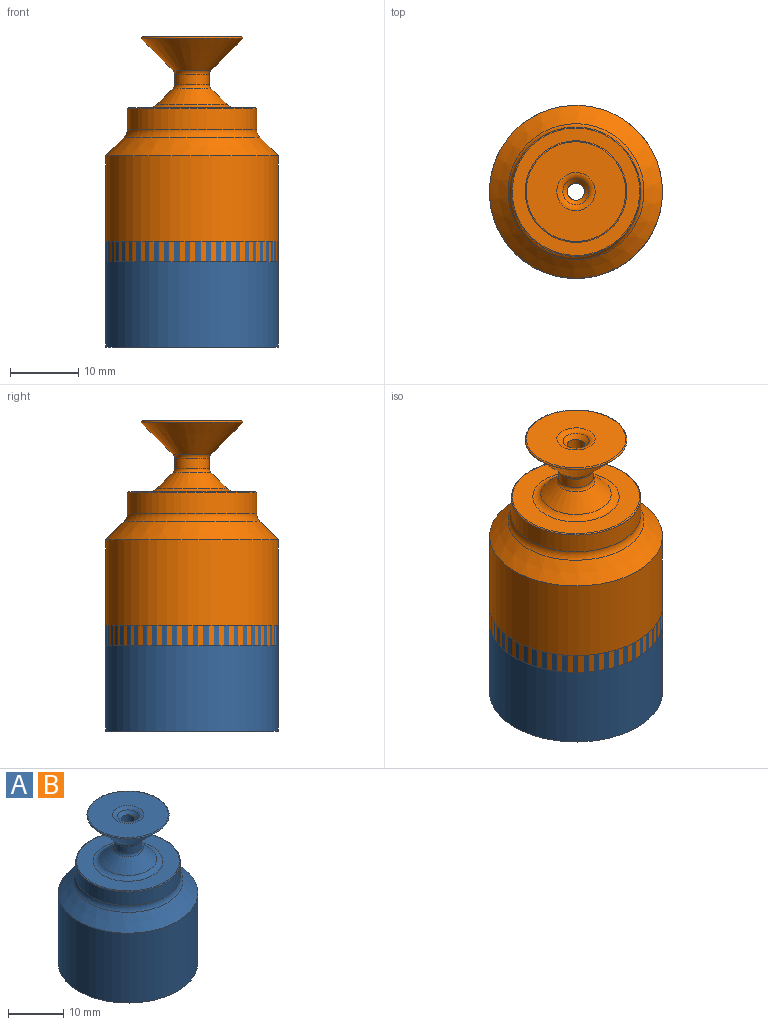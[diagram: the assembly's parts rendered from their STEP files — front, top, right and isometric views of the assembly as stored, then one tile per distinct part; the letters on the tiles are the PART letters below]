
ASSEMBLY  parts=2 mates=1
PART A: 28 faces, bbox 25.4x25.4x33 mm
  f0: cone r=7.88mm half-angle=45deg, axis (0,0,-1), area 268.9mm2, adj f4,f27
  f1: cone r=1.92mm half-angle=45deg, axis (0,0,1), area 9.2mm2, adj f5,f27
  f2: torus R=8.26mm, axis (0,0,1), area 54.3mm2, adj f3,f26
  f3: cylinder r=8.89mm len=17.78mm, axis (0,0,1), area 248.3mm2, adj f2,f4
  f4: torus R=5.45mm, axis (0,0,1), area 145mm2, adj f0,f3
  f5: torus R=2.82mm, axis (0,0,1), area 14.7mm2, adj f1,f6
  f6: plane 14.62x14.62mm, normal (0,0,1), area 143mm2, adj f5,f7
  f7: torus R=7.31mm, axis (0,0,1), area 16.7mm2, adj f6,f8
  f8: cone r=2.77mm half-angle=45deg, axis (0,0,1), area 210.4mm2, adj f7,f9
  f9: torus R=3.33mm, axis (0,0,1), area 10.2mm2, adj f8,f10
  f10: cylinder r=2.54mm len=5.08mm, axis (0,0,1), area 23.9mm2, adj f9,f11
  f11: torus R=3.33mm, axis (0,0,1), area 10.2mm2, adj f10,f12
  f12: cone r=5.18mm half-angle=45deg, axis (0,0,-1), area 85mm2, adj f11,f13
  f13: torus R=6.34mm, axis (0,0,1), area 46.7mm2, adj f12,f14
  f14: plane 18.7x18.7mm, normal (0,0,1), area 148.3mm2, adj f13,f15
  f15: torus R=9.35mm, axis (0,0,1), area 14.2mm2, adj f14,f16
  f16: cylinder r=9.5mm len=19.01mm, axis (0,0,1), area 180.5mm2, adj f15,f17
  f17: torus R=11.16mm, axis (0,0,1), area 78.8mm2, adj f16,f18
  f18: cone r=12.7mm half-angle=45deg, axis (0,0,-1), area 273.4mm2, adj f17,f19
  f19: cylinder r=12.7mm len=25.4mm, axis (0,0,1), area 1239.4mm2, adj f18,f20
  f20: plane 25.4x25.4mm, normal (0,0,-1), area 91.9mm2, adj f19,f21
  f21: cone r=10.08mm half-angle=45deg, axis (0,0,-1), area 135.5mm2, adj f20,f22
  f22: cylinder r=10.08mm len=20.15mm, axis (0,0,1), area 201mm2, adj f21,f23
  f23: torus R=8.42mm, axis (0,0,1), area 80.8mm2, adj f22,f24
  f24: cone r=7.42mm half-angle=45deg, axis (0,0,-1), area 164.3mm2, adj f23,f25
  f25: torus R=7.6mm, axis (0,0,1), area 27.9mm2, adj f24,f26
  f26: plane 16.51x16.51mm, normal (0,0,1), area 32.7mm2, adj f2,f25
  f27: cylinder r=1.27mm len=9.49mm, axis (0,0,-1), area 75.7mm2, adj f0,f1
PART B: same geometry as A
PLACE A at identity fixed
PLACE B rot(axis=(0,0,-1),147.1deg) t=(0,0,12.53)mm
MATE cylindrical B.f0 <-> A.f0  axis (0,0,-1) through (0,0,18.28)mm
